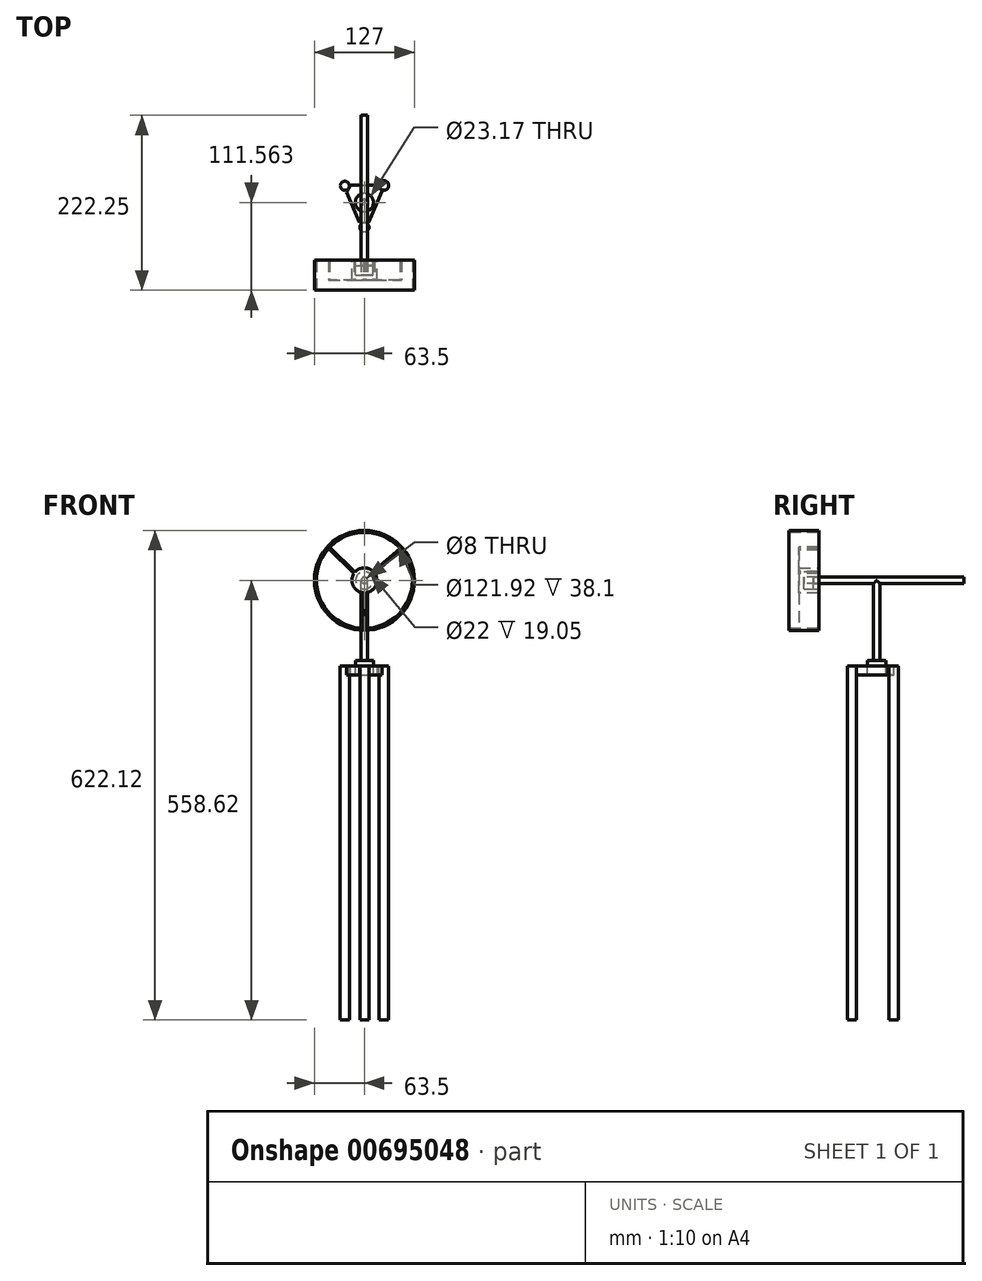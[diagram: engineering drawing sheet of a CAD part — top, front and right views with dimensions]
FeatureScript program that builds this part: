
annotation { "Feature Type Name" : "Feature", "Feature Type Description" : "" }
export const myFeature = defineFeature(function(context is Context, id is Id, definition is map)
    precondition{}
    {
        {
            var Q0;
            Q0=qCreatedBy(makeId("Front.planeOp"),FACE);
            var sketch = newSketch(context, id + "F0", { "sketchPlane" : qUnion([Q0])});
            skCircle(sketch, "E0", {"center": v(0, 0) * mm, "radius": 63.5 * mm});
            skSolve(sketch);
        }
        {
            var Q0;
            Q0=makeQuery(id+"F0.imprint","IMPRINT",FACE,{"disambiguationData":[TD([[makeQuery(id+"F0.imprint","IMPRINT",EDGE,{"derivedFrom":sQuery(id+"F0.wireOp",EDGE,"E0")}),1.0]])]});
            extrude(context, id + "F1", {"entities" : qUnion([Q0]), "depth" : 38.1 * mm, "offsetDistance" : 25.4 * mm});
        }
        {
            var Q0;
            Q0=makeQuery(id+"F1.opExtrude","CAP_FACE",FACE,{"disambiguationData":[OSD([sQuery(id+"F0.wireOp",EDGE,"E0")])],"isStart":false});
            var sketch = newSketch(context, id + "F2", { "sketchPlane" : qUnion([Q0])});
            skCircle(sketch, "E1", {"center": v(0, 0) * mm, "radius": 60.96 * mm});
            skSolve(sketch);
        }
        {
            var Q0;
            Q0=sQuery(id+"F2.wireOp",VERTEX,"E1.center");
            var Q1;
            Q1=makeQuery(id+"F1.opExtrude","SWEPT_BODY",BODY,{"disambiguationData":[OSD([sQuery(id+"F0.wireOp",EDGE,"E0")])]});
            hole(context, id + "F3", {"style" : HoleStyle.SIMPLE, "endStyle" : HoleEndStyle.THROUGH, "holeDiameter" : 121.92 * mm, "majorDiameter" : 6.35 * mm, "isTappedThrough" : true, "tappedDepth" : 12.7 * mm, "tapClearance" : 3, "locations" : qUnion([Q0]), "scope" : qUnion([Q1])});
        }
        {
            var Q0;
            Q0=qCreatedBy(makeId("Front.planeOp"),FACE);
            var sketch = newSketch(context, id + "F4", { "sketchPlane" : qUnion([Q0])});
            skCircle(sketch, "E2", {"center": v(0, 0) * mm, "radius": 15.88 * mm});
            skCircle(sketch, "E3", {"center": v(0, 0) * mm, "radius": 11 * mm});
            skLineSegment(sketch, "E4", {"start": v(0, 61.44) * mm, "end": v(0, 15.88) * mm});
            skLineSegment(sketch, "E5", {"start": v(47.53, -37.24) * mm, "end": v(12.55, -9.72) * mm});
            skLineSegment(sketch, "E6", {"start": v(-42.39, -43.15) * mm, "end": v(-12.22, -10.14) * mm});
            skSolve(sketch);
        }
        {
            var Q0;
            Q0=makeQuery(id+"F4.imprint","IMPRINT",FACE,{"disambiguationData":[TD([[makeQuery(id+"F4.imprint","IMPRINT",EDGE,{"derivedFrom":sQuery(id+"F4.wireOp",EDGE,"E2")}),1.0]])]});
            extrude(context, id + "F5", {"entities" : qUnion([Q0]), "depth" : 25.4 * mm, "offsetDistance" : 25.4 * mm});
        }
        {
            var Q0;
            Q0=makeQuery(id+"F5.opExtrude","CAP_FACE",FACE,{"disambiguationData":[OSD([sQuery(id+"F4.wireOp",EDGE,"E2"),sQuery(id+"F4.wireOp",EDGE,"E3")])],"isStart":false});
            var sketch = newSketch(context, id + "F6", { "sketchPlane" : qUnion([Q0])});
            skCircle(sketch, "E7.0", {"center": v(0, 0) * mm, "radius": 60.96 * mm});
            skCircle(sketch, "E8.0", {"center": v(0, 0) * mm, "radius": 15.88 * mm});
            skLineSegment(sketch, "E9", {"start": v(12.86, 9.3) * mm, "end": v(47.18, 38.6) * mm});
            skLineSegment(sketch, "E10", {"start": v(47.18, 38.6) * mm, "end": v(45.53, 40.53) * mm});
            skLineSegment(sketch, "E11", {"start": v(45.53, 40.53) * mm, "end": v(11.21, 11.24) * mm});
            skLineSegment(sketch, "E12", {"start": v(-1.27, -15.82) * mm, "end": v(-1.27, -60.95) * mm});
            skLineSegment(sketch, "E13", {"start": v(-1.27, -60.95) * mm, "end": v(1.27, -60.95) * mm});
            skLineSegment(sketch, "E14", {"start": v(1.27, -60.95) * mm, "end": v(1.27, -15.82) * mm});
            skLineSegment(sketch, "E15", {"start": v(1.27, -15.82) * mm, "end": v(-1.27, -15.82) * mm});
            skLineSegment(sketch, "E16", {"start": v(-11.76, 10.67) * mm, "end": v(-44.13, 42.06) * mm});
            skLineSegment(sketch, "E17", {"start": v(-44.13, 42.06) * mm, "end": v(-45.84, 40.19) * mm});
            skLineSegment(sketch, "E18", {"start": v(-45.84, 40.19) * mm, "end": v(-13.3, 8.65) * mm});
            skLineSegment(sketch, "E19", {"start": v(-13.3, 8.65) * mm, "end": v(-11.76, 10.67) * mm});
            skSolve(sketch);
        }
        {
            var Q0;
            {var subQ1=sQuery(id+"F6.wireOp",EDGE,"E16");Q0=makeQuery(id+"F6.imprint","IMPRINT",FACE,{"disambiguationData":[TD([[makeQuery(id+"F6.imprint","IMPRINT",EDGE,{"derivedFrom":subQ1}),1.0]])]});}
            var Q1;
            {var subQ0=sQuery(id+"F6.wireOp",EDGE,"E9");Q1=makeQuery(id+"F6.imprint","IMPRINT",FACE,{"disambiguationData":[TD([[makeQuery(id+"F6.imprint","IMPRINT",EDGE,{"derivedFrom":subQ0}),1.0]])]});}
            var Q2;
            {var subQ1=sQuery(id+"F6.wireOp",EDGE,"E12");Q2=makeQuery(id+"F6.imprint","IMPRINT",FACE,{"disambiguationData":[TD([[makeQuery(id+"F6.imprint","IMPRINT",EDGE,{"derivedFrom":subQ1}),1.0]])]});}
            extrude(context, id + "F7", {"entities" : qUnion([Q0, Q1, Q2]), "operationType" : NewBodyOperationType.ADD, "oppositeDirection" : true, "depth" : 25.4 * mm, "offsetDistance" : 25.4 * mm});
        }
        {
            var Q0;
            Q0=qCreatedBy(makeId("Front.planeOp"),FACE);
            var sketch = newSketch(context, id + "F8", { "sketchPlane" : qUnion([Q0])});
            skCircle(sketch, "E20", {"center": v(0, 0) * mm, "radius": 11 * mm});
            skSolve(sketch);
        }
        {
            var Q0;
            Q0=makeQuery(id+"F8.imprint","IMPRINT",FACE,{"disambiguationData":[TD([[makeQuery(id+"F8.imprint","IMPRINT",EDGE,{"derivedFrom":sQuery(id+"F8.wireOp",EDGE,"E20")}),1.0]])]});
            extrude(context, id + "F9", {"entities" : qUnion([Q0]), "depth" : 7 * mm, "offsetDistance" : 25.4 * mm});
        }
        {
            var Q0;
            Q0=qCreatedBy(makeId("Front.planeOp"),FACE);
            var sketch = newSketch(context, id + "F10", { "sketchPlane" : qUnion([Q0])});
            skPoint(sketch, "E21", {"position": v(0, 0) * mm});
            skSolve(sketch);
        }
        {
            var Q0;
            Q0=sQuery(id+"F10.wireOp",VERTEX,"E21");
            var Q1;
            Q1=makeQuery(id+"F9.opExtrude","SWEPT_BODY",BODY,{"disambiguationData":[OSD([sQuery(id+"F8.wireOp",EDGE,"E20")])]});
            hole(context, id + "F11", {"style" : HoleStyle.SIMPLE, "endStyle" : HoleEndStyle.BLIND, "oppositeDirection" : true, "holeDiameter" : 8 * mm, "majorDiameter" : 6.35 * mm, "holeDepth" : 7 * mm, "isTappedThrough" : true, "tappedDepth" : 12.7 * mm, "tapClearance" : 3, "locations" : qUnion([Q0]), "scope" : qUnion([Q1])});
        }
        {
            var Q0;
            {var subQ0=sQuery(id+"F6.wireOp",EDGE,"E8.0");Q0=makeQuery(id+"F7.boolean.opBoolean","MERGE",FACE,{"derivedFrom":[makeQuery(id+"F5.opExtrude","CAP_FACE",FACE,{"disambiguationData":[OSD([sQuery(id+"F4.wireOp",EDGE,"E2"),sQuery(id+"F4.wireOp",EDGE,"E3")])],"isStart":false}),makeQuery(id+"F7.opExtrude","CAP_FACE",FACE,{"disambiguationData":[OSD([subQ0,sQuery(id+"F6.wireOp",EDGE,"E9"),sQuery(id+"F6.wireOp",EDGE,"E10"),sQuery(id+"F6.wireOp",EDGE,"E11")])],"isStart":true}),makeQuery(id+"F7.opExtrude","CAP_FACE",FACE,{"disambiguationData":[OSD([subQ0,sQuery(id+"F6.wireOp",EDGE,"E16"),sQuery(id+"F6.wireOp",EDGE,"E17"),sQuery(id+"F6.wireOp",EDGE,"E18")])],"isStart":true}),makeQuery(id+"F7.opExtrude","CAP_FACE",FACE,{"disambiguationData":[OSD([subQ0,sQuery(id+"F6.wireOp",EDGE,"E12"),sQuery(id+"F6.wireOp",EDGE,"E13"),sQuery(id+"F6.wireOp",EDGE,"E14")])],"isStart":true})]});}
            var sketch = newSketch(context, id + "F12", { "sketchPlane" : qUnion([Q0])});
            skCircle(sketch, "E22", {"center": v(0, 0) * mm, "radius": 11 * mm});
            skSolve(sketch);
        }
        {
            var Q0;
            Q0=makeQuery(id+"F12.imprint","IMPRINT",FACE,{"disambiguationData":[TD([[makeQuery(id+"F12.imprint","IMPRINT",EDGE,{"derivedFrom":sQuery(id+"F12.wireOp",EDGE,"E22")}),1.0]])]});
            extrude(context, id + "F13", {"entities" : qUnion([Q0]), "operationType" : NewBodyOperationType.ADD, "oppositeDirection" : true, "depth" : 6.35 * mm, "offsetDistance" : 25.4 * mm});
        }
        {
            var Q0;
            Q0=makeQuery(id+"F13.opExtrude","CAP_FACE",FACE,{"disambiguationData":[OSD([sQuery(id+"F12.wireOp",EDGE,"E22")])],"isStart":false});
            var sketch = newSketch(context, id + "F14", { "sketchPlane" : qUnion([Q0])});
            skCircle(sketch, "E23", {"center": v(0, 0) * mm, "radius": 4 * mm});
            skSolve(sketch);
        }
        {
            var Q0;
            Q0=makeQuery(id+"F14.imprint","IMPRINT",FACE,{"disambiguationData":[TD([[makeQuery(id+"F14.imprint","IMPRINT",EDGE,{"derivedFrom":sQuery(id+"F14.wireOp",EDGE,"E23")}),1.0]])]});
            extrude(context, id + "F15", {"entities" : qUnion([Q0]), "depth" : 203.2 * mm, "offsetDistance" : 25.4 * mm});
        }
        {
            var Q0;
            Q0=qCreatedBy(makeId("Top.planeOp"),FACE);
            var sketch = newSketch(context, id + "F16", { "sketchPlane" : qUnion([Q0])});
            skCircle(sketch, "E24", {"center": v(0, 73.46) * mm, "radius": 4 * mm});
            skSolve(sketch);
        }
        {
            var Q0;
            Q0=makeQuery(id+"F16.imprint","IMPRINT",FACE,{"disambiguationData":[TD([[makeQuery(id+"F16.imprint","IMPRINT",EDGE,{"derivedFrom":sQuery(id+"F16.wireOp",EDGE,"E24")}),1.0]])]});
            extrude(context, id + "F17", {"entities" : qUnion([Q0]), "operationType" : NewBodyOperationType.ADD, "oppositeDirection" : true, "depth" : 101.6 * mm, "offsetDistance" : 25.4 * mm});
        }
        {
            var Q0;
            Q0=makeQuery(id+"F17.opExtrude","CAP_FACE",FACE,{"disambiguationData":[OSD([sQuery(id+"F16.wireOp",EDGE,"E24")])],"isStart":false});
            var sketch = newSketch(context, id + "F18", { "sketchPlane" : qUnion([Q0])});
            skCircle(sketch, "E25", {"center": v(0, -73.46) * mm, "radius": 11 * mm});
            skCircle(sketch, "E26", {"center": v(0, -73.46) * mm, "radius": 3.5 * mm});
            skSolve(sketch);
        }
        {
            var Q0;
            Q0=makeQuery(id+"F18.imprint","IMPRINT",FACE,{"disambiguationData":[TD([[makeQuery(id+"F18.imprint","IMPRINT",EDGE,{"derivedFrom":sQuery(id+"F18.wireOp",EDGE,"E26")}),1.0]])]});
            extrude(context, id + "F19", {"entities" : qUnion([Q0]), "operationType" : NewBodyOperationType.ADD, "depth" : 7.44 * mm, "offsetDistance" : 25.4 * mm});
        }
        {
            var Q0;
            Q0=makeQuery(id+"F19.opExtrude","CAP_FACE",FACE,{"disambiguationData":[OSD([sQuery(id+"F18.wireOp",EDGE,"E26")])],"isStart":false});
            var sketch = newSketch(context, id + "F20", { "sketchPlane" : qUnion([Q0])});
            skCircle(sketch, "E27", {"center": v(0, -73.46) * mm, "radius": 11 * mm});
            skCircle(sketch, "E28", {"center": v(0, -73.46) * mm, "radius": 3.5 * mm});
            skSolve(sketch);
        }
        {
            var Q0;
            Q0=makeQuery(id+"F20.imprint","IMPRINT",FACE,{"disambiguationData":[TD([[makeQuery(id+"F20.imprint","IMPRINT",EDGE,{"derivedFrom":sQuery(id+"F20.wireOp",EDGE,"E27")}),1.0]])]});
            extrude(context, id + "F21", {"entities" : qUnion([Q0]), "operationType" : NewBodyOperationType.ADD, "oppositeDirection" : true, "depth" : 7 * mm, "offsetDistance" : 25.4 * mm});
        }
        {
            var Q0;
            Q0=makeQuery(id+"F21.opExtrude","CAP_FACE",FACE,{"disambiguationData":[OSD([sQuery(id+"F20.wireOp",EDGE,"E27"),sQuery(id+"F20.wireOp",EDGE,"E28")])],"isStart":true});
            var sketch = newSketch(context, id + "F22", { "sketchPlane" : qUnion([Q0])});
            skCircle(sketch, "E29", {"center": v(0, -73.46) * mm, "radius": 11.58 * mm});
            skCircle(sketch, "E30", {"center": v(0, -73.46) * mm, "radius": 10.4 * mm});
            skSolve(sketch);
        }
        {
            var Q0;
            Q0=makeQuery(id+"F22.imprint","IMPRINT",FACE,{"disambiguationData":[TD([[makeQuery(id+"F22.imprint","IMPRINT",EDGE,{"derivedFrom":sQuery(id+"F22.wireOp",EDGE,"E29")}),1.0]])]});
            extrude(context, id + "F23", {"entities" : qUnion([Q0]), "operationType" : NewBodyOperationType.ADD, "oppositeDirection" : true, "depth" : 7 * mm, "offsetDistance" : 25.4 * mm});
        }
        {
            var Q0;
            Q0=makeQuery(id+"F23.opExtrude","CAP_FACE",FACE,{"disambiguationData":[OSD([sQuery(id+"F20.wireOp",EDGE,"E27"),sQuery(id+"F22.wireOp",EDGE,"E29")])],"isStart":true});
            var sketch = newSketch(context, id + "F24", { "sketchPlane" : qUnion([Q0])});
            skLineSegment(sketch, "E31", {"start": v(-26.68, -95.54) * mm, "end": v(25.7, -95.54) * mm});
            skLineSegment(sketch, "E32", {"start": v(-26.68, -95.54) * mm, "end": v(-0.49, -34.23) * mm});
            skLineSegment(sketch, "E33", {"start": v(-0.49, -34.23) * mm, "end": v(25.7, -95.54) * mm});
            skLineSegment(sketch, "E34", {"start": v(-6.35, -47.95) * mm, "end": v(5.38, -47.95) * mm});
            skLineSegment(sketch, "E35", {"start": v(16.76, -95.54) * mm, "end": v(22.33, -87.64) * mm});
            skLineSegment(sketch, "E36", {"start": v(-22.97, -86.86) * mm, "end": v(-17.41, -95.54) * mm});
            skSolve(sketch);
        }
        {
            var Q0;
            {var subQ0=sQuery(id+"F24.wireOp",EDGE,"E34");Q0=makeQuery(id+"F24.imprint","IMPRINT",FACE,{"disambiguationData":[TD([[makeQuery(id+"F24.imprint","IMPRINT",EDGE,{"derivedFrom":subQ0}),-1.0]])]});}
            extrude(context, id + "F25", {"entities" : qUnion([Q0]), "depth" : 10.87 * mm, "offsetDistance" : 25.4 * mm});
        }
        {
            var Q0;
            Q0=makeQuery(id+"F25.opExtrude","CAP_FACE",FACE,{"disambiguationData":[OSD([sQuery(id+"F22.wireOp",EDGE,"E29"),sQuery(id+"F24.wireOp",EDGE,"E31"),sQuery(id+"F24.wireOp",EDGE,"E32"),sQuery(id+"F24.wireOp",EDGE,"E33"),sQuery(id+"F24.wireOp",EDGE,"E34"),sQuery(id+"F24.wireOp",EDGE,"E35"),sQuery(id+"F24.wireOp",EDGE,"E36")])],"isStart":true});
            var sketch = newSketch(context, id + "F26", { "sketchPlane" : qUnion([Q0])});
            skCircle(sketch, "E37", {"center": v(0, 41.9) * mm, "radius": 5.81 * mm});
            skCircle(sketch, "E38", {"center": v(24.71, 95.06) * mm, "radius": 6.13 * mm});
            skCircle(sketch, "E39", {"center": v(-24.88, 94.6) * mm, "radius": 5.75 * mm});
            skSolve(sketch);
        }
        {
            var Q0;
            Q0=makeQuery(id+"F26.imprint","IMPRINT",FACE,{"disambiguationData":[TD([[makeQuery(id+"F26.imprint","IMPRINT",EDGE,{"derivedFrom":sQuery(id+"F26.wireOp",EDGE,"E39")}),1.0]])]});
            var Q1;
            Q1=makeQuery(id+"F26.imprint","IMPRINT",FACE,{"disambiguationData":[TD([[makeQuery(id+"F26.imprint","IMPRINT",EDGE,{"derivedFrom":sQuery(id+"F26.wireOp",EDGE,"E37")}),1.0]])]});
            var Q2;
            Q2=makeQuery(id+"F26.imprint","IMPRINT",FACE,{"disambiguationData":[TD([[makeQuery(id+"F26.imprint","IMPRINT",EDGE,{"derivedFrom":sQuery(id+"F26.wireOp",EDGE,"E38")}),1.0]])]});
            extrude(context, id + "F27", {"entities" : qUnion([Q0, Q1, Q2]), "oppositeDirection" : true, "depth" : 449.58 * mm, "offsetDistance" : 25.4 * mm});
        }
    });
